# Revit family: JIMMY-HQE-PANEL_LED_28W_BACKLIGHT_3360LM_4000K_UGR17_595X593
name_source: partatom
category: Lighting Fixtures
units: mm (PartAtom-declared; Revit-internal decimal feet)

## family parameters
Always vertical = Yes
Cut with Voids When Loaded = No
Host = Ceiling
Light Source = Yes
OmniClass Number = 23.80.70.11
OmniClass Title = Luminaries for Internal Lighting
Part Type = Normal
Room Calculation Point = No
Round Connector Dimension = Use Diameter
Shared = No

## types (1)
- Type 1
    Alimentation Driver = 220-240V AC
    Alimentation luminaire = 33-40V dc / 1000 mA
    Angle d'éclairage = 90°
    Color Filter = 16777215
    Default Elevation = 0 mm  [stored 0 ft]
    Diffuseur = Diffuseur prismatique
    Dimensions = 595 x 595 x 30 mm
    Dimensions d’encastrement = 595 x 595 x 30 mm
    Dimming Lamp Color Temperature Shift = <None>
    Driver = Driver Lifud 750mA no-flicker
 Driver classe 2 marque Lifud no-flicker avec connecteur rapide/ option DALI
 connecteur rapide/ op�on DALI
    Durée de vie = 50 000 heures
    Emit Shape Visible in Rendering = No
    Emit from Rectangle Length = 1219 mm
    Emit from Rectangle Width = 610 mm
    IRC = >80
    Lamp = LED San’an 100lm/W
    Maintien du flux = L80B10 (50 000 heures)
    Manufacturer = Lucera - Lucera (c) 06/01/2021 16:37:56 +01:00
    Matériau = aluminium laqué blanc
    Photometric Web File = google_eulumdat_converter.ies
    Puissance nominale = 28W
    SDCM = <3
    Tilt Angle = 90.00°
    Type = LED
    Type de lampe = LED San'an
    URL = https://www.lucera.fr
    Wattage Comments = 40W

note: [stored X ft] marks values corroborated as IEEE doubles in the binary element streams (Revit-internal decimal feet)

## geometry (parser evidence)
native form markers: Sweep x2
no freeform markers — native parametric forms only
